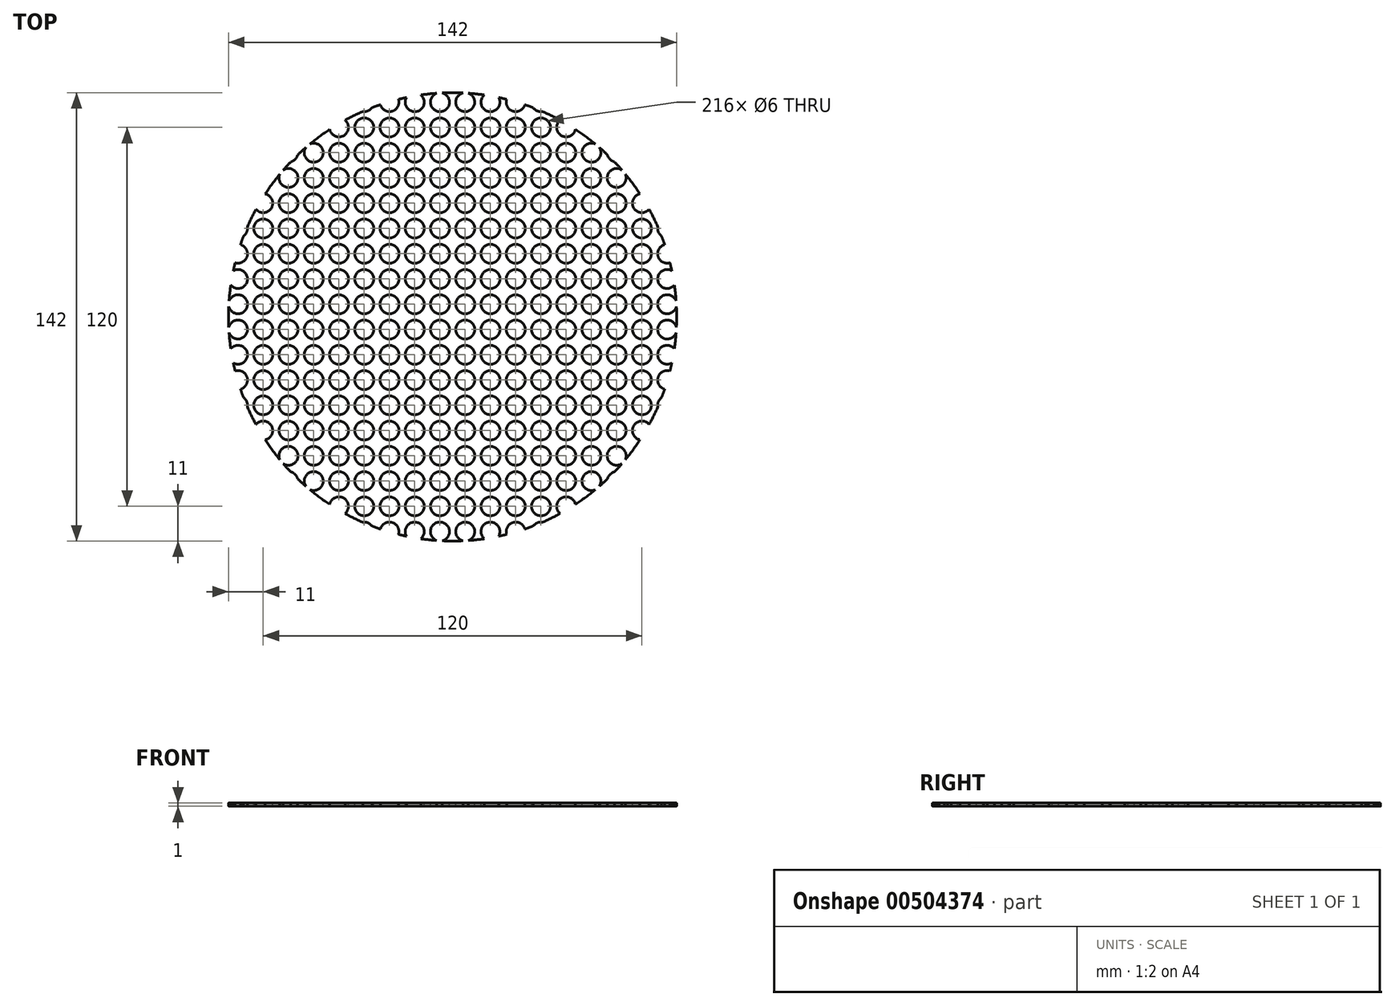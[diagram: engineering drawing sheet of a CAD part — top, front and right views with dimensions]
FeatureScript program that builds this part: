
annotation { "Feature Type Name" : "Feature", "Feature Type Description" : "" }
export const myFeature = defineFeature(function(context is Context, id is Id, definition is map)
    precondition{}
    {
        {
            var Q0;
            Q0=qCreatedBy(makeId("Top.planeOp"),FACE);
            var sketch = newSketch(context, id + "F0", { "sketchPlane" : qUnion([Q0])});
            skCircle(sketch, "E0.0", {"center": v(0, 0) * mm, "radius": 71 * mm});
            skSolve(sketch);
        }
        {
            var Q0;
            Q0 = qSketchRegion(id + "F0", true);
            extrude(context, id + "F1", {"entities" : qUnion([Q0]), "oppositeDirection" : true, "depth" : 1 * mm, "offsetDistance" : 25 * mm});
        }
        {
            var Q0;
            Q0=qCreatedBy(makeId("Top.planeOp"),FACE);
            var sketch = newSketch(context, id + "F2", { "sketchPlane" : qUnion([Q0])});
            skCircle(sketch, "E1", {"center": v(0, 0) * mm, "radius": 71 * mm, "construction": true});
            skLineSegment(sketch, "E2", {"start": v(-4, 70.89) * mm, "end": v(-4, -70.89) * mm, "construction": true});
            skLineSegment(sketch, "E3", {"start": v(-12, 69.98) * mm, "end": v(-12, -69.98) * mm, "construction": true});
            skLineSegment(sketch, "E4", {"start": v(-20, 68.12) * mm, "end": v(-20, -68.12) * mm, "construction": true});
            skLineSegment(sketch, "E5", {"start": v(-28, 65.25) * mm, "end": v(-28, -65.25) * mm, "construction": true});
            skLineSegment(sketch, "E6.MirrorCS", {"start": v(-36, 68.12) * mm, "end": v(-36, -68.12) * mm, "construction": true});
            skLineSegment(sketch, "E7.MirrorCS", {"start": v(-44, 69.98) * mm, "end": v(-44, -69.98) * mm, "construction": true});
            skLineSegment(sketch, "E8.MirrorCS", {"start": v(-52, 70.89) * mm, "end": v(-52, -70.89) * mm, "construction": true});
            skLineSegment(sketch, "E9.MirrorCS", {"start": v(-60, 69.98) * mm, "end": v(-60, -69.98) * mm, "construction": true});
            skLineSegment(sketch, "E10.MirrorCS", {"start": v(-68, 68.12) * mm, "end": v(-68, -68.12) * mm, "construction": true});
            skLineSegment(sketch, "E11.MirrorCS", {"start": v(4, 70.89) * mm, "end": v(4, -70.89) * mm, "construction": true});
            skLineSegment(sketch, "E12.MirrorCS", {"start": v(12, 69.98) * mm, "end": v(12, -69.98) * mm, "construction": true});
            skLineSegment(sketch, "E13.MirrorCS", {"start": v(20, 68.12) * mm, "end": v(20, -68.12) * mm, "construction": true});
            skLineSegment(sketch, "E14.MirrorCS", {"start": v(28, 65.25) * mm, "end": v(28, -65.25) * mm, "construction": true});
            skLineSegment(sketch, "E15.MirrorCS", {"start": v(36, 68.12) * mm, "end": v(36, -68.12) * mm, "construction": true});
            skLineSegment(sketch, "E16.MirrorCS", {"start": v(44, 69.98) * mm, "end": v(44, -69.98) * mm, "construction": true});
            skLineSegment(sketch, "E17.MirrorCS", {"start": v(52, 70.89) * mm, "end": v(52, -70.89) * mm, "construction": true});
            skLineSegment(sketch, "E18.MirrorCS", {"start": v(60, 69.98) * mm, "end": v(60, -69.98) * mm, "construction": true});
            skLineSegment(sketch, "E19.MirrorCS", {"start": v(68, 68.12) * mm, "end": v(68, -68.12) * mm, "construction": true});
            skLineSegment(sketch, "E20", {"start": v(-70.89, 4) * mm, "end": v(70.89, 4) * mm, "construction": true});
            skLineSegment(sketch, "E21", {"start": v(-69.98, 12) * mm, "end": v(69.98, 12) * mm, "construction": true});
            skLineSegment(sketch, "E22", {"start": v(-68.12, 20) * mm, "end": v(68.12, 20) * mm});
            skLineSegment(sketch, "E23.MirrorCS", {"start": v(-69.98, 28) * mm, "end": v(69.98, 28) * mm, "construction": true});
            skLineSegment(sketch, "E24.MirrorCS", {"start": v(-70.89, 36) * mm, "end": v(70.89, 36) * mm, "construction": true});
            skLineSegment(sketch, "E25.MirrorCS", {"start": v(-69.98, 44) * mm, "end": v(69.98, 44) * mm, "construction": true});
            skLineSegment(sketch, "E26.MirrorCS", {"start": v(-68.12, 52) * mm, "end": v(68.12, 52) * mm, "construction": true});
            skLineSegment(sketch, "E27.MirrorCS", {"start": v(-69.98, 60) * mm, "end": v(69.98, 60) * mm, "construction": true});
            skLineSegment(sketch, "E28.MirrorCS", {"start": v(-70.89, 68) * mm, "end": v(70.89, 68) * mm, "construction": true});
            skLineSegment(sketch, "E29.MirrorCS", {"start": v(-69.98, -12) * mm, "end": v(69.98, -12) * mm, "construction": true});
            skLineSegment(sketch, "E30.MirrorCS", {"start": v(-68.12, -20) * mm, "end": v(68.12, -20) * mm, "construction": true});
            skLineSegment(sketch, "E31.MirrorCS", {"start": v(-69.98, -28) * mm, "end": v(69.98, -28) * mm, "construction": true});
            skLineSegment(sketch, "E32.MirrorCS", {"start": v(-70.89, -36) * mm, "end": v(70.89, -36) * mm, "construction": true});
            skLineSegment(sketch, "E33.MirrorCS", {"start": v(-69.98, -44) * mm, "end": v(69.98, -44) * mm, "construction": true});
            skLineSegment(sketch, "E34.MirrorCS", {"start": v(-68.12, -52) * mm, "end": v(68.12, -52) * mm, "construction": true});
            skLineSegment(sketch, "E35.MirrorCS", {"start": v(-69.98, -60) * mm, "end": v(69.98, -60) * mm, "construction": true});
            skLineSegment(sketch, "E36.MirrorCS", {"start": v(-70.89, -68) * mm, "end": v(70.89, -68) * mm, "construction": true});
            skLineSegment(sketch, "E37.MirrorCS", {"start": v(-70.89, -4) * mm, "end": v(70.89, -4) * mm, "construction": true});
            skCircle(sketch, "E38", {"center": v(-12, 4) * mm, "radius": 3 * mm});
            skCircle(sketch, "E39.MirrorC", {"center": v(-28, 4) * mm, "radius": 3 * mm});
            skCircle(sketch, "E40", {"center": v(-20, 4) * mm, "radius": 3 * mm});
            skCircle(sketch, "E41.MirrorC", {"center": v(-36, 4) * mm, "radius": 3 * mm});
            skCircle(sketch, "E42.MirrorC", {"center": v(-44, 4) * mm, "radius": 3 * mm});
            skCircle(sketch, "E43.MirrorC", {"center": v(-52, 4) * mm, "radius": 3 * mm});
            skCircle(sketch, "E44.MirrorC", {"center": v(-60, 4) * mm, "radius": 3 * mm});
            skCircle(sketch, "E45.MirrorC", {"center": v(-68, 4) * mm, "radius": 3 * mm});
            skCircle(sketch, "E46.MirrorC", {"center": v(-4, 4) * mm, "radius": 3 * mm});
            skCircle(sketch, "E47.MirrorC", {"center": v(-4, -4) * mm, "radius": 3 * mm});
            skCircle(sketch, "E48.MirrorC", {"center": v(-12, -4) * mm, "radius": 3 * mm});
            skCircle(sketch, "E49.MirrorC", {"center": v(-20, -4) * mm, "radius": 3 * mm});
            skCircle(sketch, "E50.MirrorC", {"center": v(-28, -4) * mm, "radius": 3 * mm});
            skCircle(sketch, "E51.MirrorC", {"center": v(-36, -4) * mm, "radius": 3 * mm});
            skCircle(sketch, "E52.MirrorC", {"center": v(-44, -4) * mm, "radius": 3 * mm});
            skCircle(sketch, "E53.MirrorC", {"center": v(-52, -4) * mm, "radius": 3 * mm});
            skCircle(sketch, "E54.MirrorC", {"center": v(-60, -4) * mm, "radius": 3 * mm});
            skCircle(sketch, "E55.MirrorC", {"center": v(-68, -4) * mm, "radius": 3 * mm});
            skCircle(sketch, "E56.MirrorC", {"center": v(-4, 20) * mm, "radius": 3 * mm});
            skCircle(sketch, "E57.MirrorC", {"center": v(-4, 28) * mm, "radius": 3 * mm});
            skCircle(sketch, "E58.MirrorC", {"center": v(-12, 28) * mm, "radius": 3 * mm});
            skCircle(sketch, "E59.MirrorC", {"center": v(-12, 20) * mm, "radius": 3 * mm});
            skCircle(sketch, "E60.MirrorC", {"center": v(-20, 20) * mm, "radius": 3 * mm});
            skCircle(sketch, "E61.MirrorC", {"center": v(-20, 28) * mm, "radius": 3 * mm});
            skCircle(sketch, "E62.MirrorC", {"center": v(-28, 20) * mm, "radius": 3 * mm});
            skCircle(sketch, "E63.MirrorC", {"center": v(-28, 28) * mm, "radius": 3 * mm});
            skCircle(sketch, "E64.MirrorC", {"center": v(-36, 20) * mm, "radius": 3 * mm});
            skCircle(sketch, "E65.MirrorC", {"center": v(-36, 28) * mm, "radius": 3 * mm});
            skCircle(sketch, "E66.MirrorC", {"center": v(-44, 20) * mm, "radius": 3 * mm});
            skCircle(sketch, "E67.MirrorC", {"center": v(-44, 28) * mm, "radius": 3 * mm});
            skCircle(sketch, "E68.MirrorC", {"center": v(-52, 28) * mm, "radius": 3 * mm});
            skCircle(sketch, "E69.MirrorC", {"center": v(-52, 20) * mm, "radius": 3 * mm});
            skCircle(sketch, "E70.MirrorC", {"center": v(-60, 20) * mm, "radius": 3 * mm});
            skCircle(sketch, "E71.MirrorC", {"center": v(-68, 20) * mm, "radius": 3 * mm});
            skCircle(sketch, "E72.MirrorC", {"center": v(-4, 12) * mm, "radius": 3 * mm});
            skCircle(sketch, "E73.MirrorC", {"center": v(-12, 12) * mm, "radius": 3 * mm});
            skCircle(sketch, "E74.MirrorC", {"center": v(-20, 12) * mm, "radius": 3 * mm});
            skCircle(sketch, "E75.MirrorC", {"center": v(-28, 12) * mm, "radius": 3 * mm});
            skCircle(sketch, "E76.MirrorC", {"center": v(-36, 12) * mm, "radius": 3 * mm});
            skCircle(sketch, "E77.MirrorC", {"center": v(-44, 12) * mm, "radius": 3 * mm});
            skCircle(sketch, "E78.MirrorC", {"center": v(-52, 12) * mm, "radius": 3 * mm});
            skCircle(sketch, "E79.MirrorC", {"center": v(-60, 12) * mm, "radius": 3 * mm});
            skLineSegment(sketch, "E80.MirrorCS", {"start": v(-60, -61.98) * mm, "end": v(-60, 77.98) * mm, "construction": true});
            skCircle(sketch, "E81.MirrorC", {"center": v(-68, 12) * mm, "radius": 3 * mm});
            skCircle(sketch, "E82.MirrorC", {"center": v(-68, 28) * mm, "radius": 3 * mm});
            skCircle(sketch, "E83.MirrorC", {"center": v(-60, 28) * mm, "radius": 3 * mm});
            skCircle(sketch, "E84.MirrorC", {"center": v(-52, 44) * mm, "radius": 3 * mm});
            skCircle(sketch, "E85.MirrorC", {"center": v(-36, 44) * mm, "radius": 3 * mm});
            skCircle(sketch, "E86.MirrorC", {"center": v(-52, 36) * mm, "radius": 3 * mm});
            skCircle(sketch, "E87.MirrorC", {"center": v(-44, 36) * mm, "radius": 3 * mm});
            skCircle(sketch, "E88.MirrorC", {"center": v(-44, 44) * mm, "radius": 3 * mm});
            skCircle(sketch, "E89.MirrorC", {"center": v(-28, 44) * mm, "radius": 3 * mm});
            skCircle(sketch, "E90.MirrorC", {"center": v(-60, 36) * mm, "radius": 3 * mm});
            skCircle(sketch, "E91.MirrorC", {"center": v(-36, 36) * mm, "radius": 3 * mm});
            skCircle(sketch, "E92.MirrorC", {"center": v(-28, 36) * mm, "radius": 3 * mm});
            skCircle(sketch, "E93.MirrorC", {"center": v(-20, 36) * mm, "radius": 3 * mm});
            skCircle(sketch, "E94.MirrorC", {"center": v(-68, 44) * mm, "radius": 3 * mm});
            skCircle(sketch, "E95.MirrorC", {"center": v(-4, 36) * mm, "radius": 3 * mm});
            skCircle(sketch, "E96.MirrorC", {"center": v(-60, 44) * mm, "radius": 3 * mm});
            skCircle(sketch, "E97.MirrorC", {"center": v(-12, 36) * mm, "radius": 3 * mm});
            skCircle(sketch, "E98.MirrorC", {"center": v(-4, 44) * mm, "radius": 3 * mm});
            skCircle(sketch, "E99.MirrorC", {"center": v(-12, 44) * mm, "radius": 3 * mm});
            skCircle(sketch, "E100.MirrorC", {"center": v(-20, 44) * mm, "radius": 3 * mm});
            skCircle(sketch, "E101.MirrorC", {"center": v(-68, 36) * mm, "radius": 3 * mm});
            skCircle(sketch, "E102.MirrorC", {"center": v(-4, 60) * mm, "radius": 3 * mm});
            skCircle(sketch, "E103.MirrorC", {"center": v(-68, 60) * mm, "radius": 3 * mm});
            skCircle(sketch, "E104.MirrorC", {"center": v(-52, 60) * mm, "radius": 3 * mm});
            skCircle(sketch, "E105.MirrorC", {"center": v(-44, 60) * mm, "radius": 3 * mm});
            skCircle(sketch, "E106.MirrorC", {"center": v(-36, 60) * mm, "radius": 3 * mm});
            skCircle(sketch, "E107.MirrorC", {"center": v(-20, 60) * mm, "radius": 3 * mm});
            skCircle(sketch, "E108.MirrorC", {"center": v(-60, 60) * mm, "radius": 3 * mm});
            skCircle(sketch, "E109.MirrorC", {"center": v(-28, 60) * mm, "radius": 3 * mm});
            skCircle(sketch, "E110.MirrorC", {"center": v(-12, 60) * mm, "radius": 3 * mm});
            skCircle(sketch, "E111.MirrorC", {"center": v(-36, 52) * mm, "radius": 3 * mm});
            skCircle(sketch, "E112.MirrorC", {"center": v(-68, 52) * mm, "radius": 3 * mm});
            skCircle(sketch, "E113.MirrorC", {"center": v(-44, 68) * mm, "radius": 3 * mm});
            skCircle(sketch, "E114.MirrorC", {"center": v(-52, 52) * mm, "radius": 3 * mm});
            skCircle(sketch, "E115.MirrorC", {"center": v(-4, 52) * mm, "radius": 3 * mm});
            skCircle(sketch, "E116.MirrorC", {"center": v(-12, 68) * mm, "radius": 3 * mm});
            skCircle(sketch, "E117.MirrorC", {"center": v(-12, 52) * mm, "radius": 3 * mm});
            skCircle(sketch, "E118.MirrorC", {"center": v(-4, 68) * mm, "radius": 3 * mm});
            skCircle(sketch, "E119.MirrorC", {"center": v(-60, 52) * mm, "radius": 3 * mm});
            skCircle(sketch, "E120.MirrorC", {"center": v(-60, 68) * mm, "radius": 3 * mm});
            skCircle(sketch, "E121.MirrorC", {"center": v(-52, 68) * mm, "radius": 3 * mm});
            skCircle(sketch, "E122.MirrorC", {"center": v(-28, 52) * mm, "radius": 3 * mm});
            skCircle(sketch, "E123.MirrorC", {"center": v(-28, 68) * mm, "radius": 3 * mm});
            skCircle(sketch, "E124.MirrorC", {"center": v(-68, 68) * mm, "radius": 3 * mm});
            skCircle(sketch, "E125.MirrorC", {"center": v(-36, 68) * mm, "radius": 3 * mm});
            skCircle(sketch, "E126.MirrorC", {"center": v(-44, 52) * mm, "radius": 3 * mm});
            skCircle(sketch, "E127.MirrorC", {"center": v(-20, 68) * mm, "radius": 3 * mm});
            skCircle(sketch, "E128.MirrorC", {"center": v(-20, 52) * mm, "radius": 3 * mm});
            skCircle(sketch, "E129.MirrorC", {"center": v(52, -4) * mm, "radius": 3 * mm});
            skCircle(sketch, "E130.MirrorC", {"center": v(52, 44) * mm, "radius": 3 * mm});
            skCircle(sketch, "E131.MirrorC", {"center": v(44, 28) * mm, "radius": 3 * mm});
            skCircle(sketch, "E132.MirrorC", {"center": v(68, 28) * mm, "radius": 3 * mm});
            skCircle(sketch, "E133.MirrorC", {"center": v(52, 28) * mm, "radius": 3 * mm});
            skCircle(sketch, "E134.MirrorC", {"center": v(68, 60) * mm, "radius": 3 * mm});
            skCircle(sketch, "E135.MirrorC", {"center": v(36, 28) * mm, "radius": 3 * mm});
            skCircle(sketch, "E136.MirrorC", {"center": v(4, 60) * mm, "radius": 3 * mm});
            skCircle(sketch, "E137.MirrorC", {"center": v(60, 28) * mm, "radius": 3 * mm});
            skCircle(sketch, "E138.MirrorC", {"center": v(36, 60) * mm, "radius": 3 * mm});
            skCircle(sketch, "E139.MirrorC", {"center": v(28, 28) * mm, "radius": 3 * mm});
            skCircle(sketch, "E140.MirrorC", {"center": v(52, 60) * mm, "radius": 3 * mm});
            skCircle(sketch, "E141.MirrorC", {"center": v(12, 60) * mm, "radius": 3 * mm});
            skCircle(sketch, "E142.MirrorC", {"center": v(4, 28) * mm, "radius": 3 * mm});
            skCircle(sketch, "E143.MirrorC", {"center": v(60, 60) * mm, "radius": 3 * mm});
            skCircle(sketch, "E144.MirrorC", {"center": v(44, 60) * mm, "radius": 3 * mm});
            skCircle(sketch, "E145.MirrorC", {"center": v(12, 28) * mm, "radius": 3 * mm});
            skCircle(sketch, "E146.MirrorC", {"center": v(28, 60) * mm, "radius": 3 * mm});
            skCircle(sketch, "E147.MirrorC", {"center": v(20, 28) * mm, "radius": 3 * mm});
            skCircle(sketch, "E148.MirrorC", {"center": v(20, 60) * mm, "radius": 3 * mm});
            skCircle(sketch, "E149.MirrorC", {"center": v(52, 52) * mm, "radius": 3 * mm});
            skCircle(sketch, "E150.MirrorC", {"center": v(36, 68) * mm, "radius": 3 * mm});
            skCircle(sketch, "E151.MirrorC", {"center": v(36, -4) * mm, "radius": 3 * mm});
            skCircle(sketch, "E152.MirrorC", {"center": v(68, 12) * mm, "radius": 3 * mm});
            skCircle(sketch, "E153.MirrorC", {"center": v(36, 36) * mm, "radius": 3 * mm});
            skCircle(sketch, "E154.MirrorC", {"center": v(68, 36) * mm, "radius": 3 * mm});
            skCircle(sketch, "E155.MirrorC", {"center": v(44, 68) * mm, "radius": 3 * mm});
            skCircle(sketch, "E156.MirrorC", {"center": v(68, 68) * mm, "radius": 3 * mm});
            skCircle(sketch, "E157.MirrorC", {"center": v(28, -4) * mm, "radius": 3 * mm});
            skCircle(sketch, "E158.MirrorC", {"center": v(44, 20) * mm, "radius": 3 * mm});
            skCircle(sketch, "E159.MirrorC", {"center": v(20, -4) * mm, "radius": 3 * mm});
            skCircle(sketch, "E160.MirrorC", {"center": v(60, 36) * mm, "radius": 3 * mm});
            skCircle(sketch, "E161.MirrorC", {"center": v(68, 52) * mm, "radius": 3 * mm});
            skCircle(sketch, "E162.MirrorC", {"center": v(44, -4) * mm, "radius": 3 * mm});
            skCircle(sketch, "E163.MirrorC", {"center": v(44, 52) * mm, "radius": 3 * mm});
            skCircle(sketch, "E164.MirrorC", {"center": v(4, 52) * mm, "radius": 3 * mm});
            skCircle(sketch, "E165.MirrorC", {"center": v(20, 20) * mm, "radius": 3 * mm});
            skCircle(sketch, "E166.MirrorC", {"center": v(60, 4) * mm, "radius": 3 * mm});
            skCircle(sketch, "E167.MirrorC", {"center": v(4, 44) * mm, "radius": 3 * mm});
            skCircle(sketch, "E168.MirrorC", {"center": v(44, 36) * mm, "radius": 3 * mm});
            skCircle(sketch, "E169.MirrorC", {"center": v(36, 12) * mm, "radius": 3 * mm});
            skCircle(sketch, "E170.MirrorC", {"center": v(60, 68) * mm, "radius": 3 * mm});
            skCircle(sketch, "E171.MirrorC", {"center": v(52, 12) * mm, "radius": 3 * mm});
            skCircle(sketch, "E172.MirrorC", {"center": v(28, 20) * mm, "radius": 3 * mm});
            skCircle(sketch, "E173.MirrorC", {"center": v(4, 4) * mm, "radius": 3 * mm});
            skCircle(sketch, "E174.MirrorC", {"center": v(28, 52) * mm, "radius": 3 * mm});
            skCircle(sketch, "E175.MirrorC", {"center": v(52, 20) * mm, "radius": 3 * mm});
            skCircle(sketch, "E176.MirrorC", {"center": v(12, 44) * mm, "radius": 3 * mm});
            skCircle(sketch, "E177.MirrorC", {"center": v(20, 68) * mm, "radius": 3 * mm});
            skCircle(sketch, "E178.MirrorC", {"center": v(28, 44) * mm, "radius": 3 * mm});
            skCircle(sketch, "E179.MirrorC", {"center": v(12, 36) * mm, "radius": 3 * mm});
            skCircle(sketch, "E180.MirrorC", {"center": v(52, 4) * mm, "radius": 3 * mm});
            skCircle(sketch, "E181.MirrorC", {"center": v(12, 20) * mm, "radius": 3 * mm});
            skCircle(sketch, "E182.MirrorC", {"center": v(28, 68) * mm, "radius": 3 * mm});
            skCircle(sketch, "E183.MirrorC", {"center": v(4, 68) * mm, "radius": 3 * mm});
            skCircle(sketch, "E184.MirrorC", {"center": v(36, 4) * mm, "radius": 3 * mm});
            skCircle(sketch, "E185.MirrorC", {"center": v(4, -4) * mm, "radius": 3 * mm});
            skCircle(sketch, "E186.MirrorC", {"center": v(12, 12) * mm, "radius": 3 * mm});
            skCircle(sketch, "E187.MirrorC", {"center": v(52, 36) * mm, "radius": 3 * mm});
            skCircle(sketch, "E188.MirrorC", {"center": v(60, 52) * mm, "radius": 3 * mm});
            skCircle(sketch, "E189.MirrorC", {"center": v(4, 36) * mm, "radius": 3 * mm});
            skCircle(sketch, "E190.MirrorC", {"center": v(60, 20) * mm, "radius": 3 * mm});
            skCircle(sketch, "E191.MirrorC", {"center": v(60, -4) * mm, "radius": 3 * mm});
            skCircle(sketch, "E192.MirrorC", {"center": v(36, 20) * mm, "radius": 3 * mm});
            skCircle(sketch, "E193.MirrorC", {"center": v(28, 12) * mm, "radius": 3 * mm});
            skCircle(sketch, "E194.MirrorC", {"center": v(28, 36) * mm, "radius": 3 * mm});
            skCircle(sketch, "E195.MirrorC", {"center": v(68, 20) * mm, "radius": 3 * mm});
            skCircle(sketch, "E196.MirrorC", {"center": v(12, -4) * mm, "radius": 3 * mm});
            skCircle(sketch, "E197.MirrorC", {"center": v(44, 12) * mm, "radius": 3 * mm});
            skCircle(sketch, "E198.MirrorC", {"center": v(20, 52) * mm, "radius": 3 * mm});
            skCircle(sketch, "E199.MirrorC", {"center": v(60, 44) * mm, "radius": 3 * mm});
            skCircle(sketch, "E200.MirrorC", {"center": v(4, 20) * mm, "radius": 3 * mm});
            skCircle(sketch, "E201.MirrorC", {"center": v(20, 4) * mm, "radius": 3 * mm});
            skCircle(sketch, "E202.MirrorC", {"center": v(36, 44) * mm, "radius": 3 * mm});
            skCircle(sketch, "E203.MirrorC", {"center": v(44, 44) * mm, "radius": 3 * mm});
            skCircle(sketch, "E204.MirrorC", {"center": v(68, 4) * mm, "radius": 3 * mm});
            skCircle(sketch, "E205.MirrorC", {"center": v(20, 44) * mm, "radius": 3 * mm});
            skCircle(sketch, "E206.MirrorC", {"center": v(4, 12) * mm, "radius": 3 * mm});
            skCircle(sketch, "E207.MirrorC", {"center": v(68, 44) * mm, "radius": 3 * mm});
            skCircle(sketch, "E208.MirrorC", {"center": v(12, 4) * mm, "radius": 3 * mm});
            skCircle(sketch, "E209.MirrorC", {"center": v(28, 4) * mm, "radius": 3 * mm});
            skCircle(sketch, "E210.MirrorC", {"center": v(60, 12) * mm, "radius": 3 * mm});
            skCircle(sketch, "E211.MirrorC", {"center": v(36, 52) * mm, "radius": 3 * mm});
            skCircle(sketch, "E212.MirrorC", {"center": v(52, 68) * mm, "radius": 3 * mm});
            skCircle(sketch, "E213.MirrorC", {"center": v(20, 12) * mm, "radius": 3 * mm});
            skCircle(sketch, "E214.MirrorC", {"center": v(68, -4) * mm, "radius": 3 * mm});
            skCircle(sketch, "E215.MirrorC", {"center": v(20, 36) * mm, "radius": 3 * mm});
            skCircle(sketch, "E216.MirrorC", {"center": v(44, 4) * mm, "radius": 3 * mm});
            skCircle(sketch, "E217.MirrorC", {"center": v(12, 52) * mm, "radius": 3 * mm});
            skCircle(sketch, "E218.MirrorC", {"center": v(12, 68) * mm, "radius": 3 * mm});
            skLineSegment(sketch, "E219.MirrorCS", {"start": v(70.89, -4) * mm, "end": v(-70.89, -4) * mm});
            skCircle(sketch, "E220.MirrorC", {"center": v(-52, -52) * mm, "radius": 3 * mm});
            skCircle(sketch, "E221.MirrorC", {"center": v(52, -52) * mm, "radius": 3 * mm});
            skCircle(sketch, "E222.MirrorC", {"center": v(-68, -68) * mm, "radius": 3 * mm});
            skCircle(sketch, "E223.MirrorC", {"center": v(4, -68) * mm, "radius": 3 * mm});
            skCircle(sketch, "E224.MirrorC", {"center": v(36, -36) * mm, "radius": 3 * mm});
            skCircle(sketch, "E225.MirrorC", {"center": v(20, -36) * mm, "radius": 3 * mm});
            skCircle(sketch, "E226.MirrorC", {"center": v(-28, -36) * mm, "radius": 3 * mm});
            skCircle(sketch, "E227.MirrorC", {"center": v(-12, -68) * mm, "radius": 3 * mm});
            skCircle(sketch, "E228.MirrorC", {"center": v(-20, -36) * mm, "radius": 3 * mm});
            skCircle(sketch, "E229.MirrorC", {"center": v(52, -68) * mm, "radius": 3 * mm});
            skCircle(sketch, "E230.MirrorC", {"center": v(-20, -68) * mm, "radius": 3 * mm});
            skCircle(sketch, "E231.MirrorC", {"center": v(-12, -36) * mm, "radius": 3 * mm});
            skCircle(sketch, "E232.MirrorC", {"center": v(60, -36) * mm, "radius": 3 * mm});
            skCircle(sketch, "E233.MirrorC", {"center": v(28, -68) * mm, "radius": 3 * mm});
            skCircle(sketch, "E234.MirrorC", {"center": v(-52, -68) * mm, "radius": 3 * mm});
            skCircle(sketch, "E235.MirrorC", {"center": v(-44, -36) * mm, "radius": 3 * mm});
            skCircle(sketch, "E236.MirrorC", {"center": v(36, -68) * mm, "radius": 3 * mm});
            skCircle(sketch, "E237.MirrorC", {"center": v(-36, -36) * mm, "radius": 3 * mm});
            skCircle(sketch, "E238.MirrorC", {"center": v(52, -36) * mm, "radius": 3 * mm});
            skCircle(sketch, "E239.MirrorC", {"center": v(44, -36) * mm, "radius": 3 * mm});
            skCircle(sketch, "E240.MirrorC", {"center": v(28, -36) * mm, "radius": 3 * mm});
            skCircle(sketch, "E241.MirrorC", {"center": v(44, -68) * mm, "radius": 3 * mm});
            skCircle(sketch, "E242.MirrorC", {"center": v(-4, -68) * mm, "radius": 3 * mm});
            skCircle(sketch, "E243.MirrorC", {"center": v(-4, -36) * mm, "radius": 3 * mm});
            skCircle(sketch, "E244.MirrorC", {"center": v(-68, -36) * mm, "radius": 3 * mm});
            skCircle(sketch, "E245.MirrorC", {"center": v(-52, -36) * mm, "radius": 3 * mm});
            skCircle(sketch, "E246.MirrorC", {"center": v(12, -68) * mm, "radius": 3 * mm});
            skCircle(sketch, "E247.MirrorC", {"center": v(-60, -36) * mm, "radius": 3 * mm});
            skCircle(sketch, "E248.MirrorC", {"center": v(-36, -68) * mm, "radius": 3 * mm});
            skCircle(sketch, "E249.MirrorC", {"center": v(4, -36) * mm, "radius": 3 * mm});
            skCircle(sketch, "E250.MirrorC", {"center": v(12, -36) * mm, "radius": 3 * mm});
            skCircle(sketch, "E251.MirrorC", {"center": v(-60, -68) * mm, "radius": 3 * mm});
            skCircle(sketch, "E252.MirrorC", {"center": v(68, -68) * mm, "radius": 3 * mm});
            skCircle(sketch, "E253.MirrorC", {"center": v(68, -36) * mm, "radius": 3 * mm});
            skCircle(sketch, "E254.MirrorC", {"center": v(-44, -68) * mm, "radius": 3 * mm});
            skCircle(sketch, "E255.MirrorC", {"center": v(-28, -68) * mm, "radius": 3 * mm});
            skCircle(sketch, "E256.MirrorC", {"center": v(20, -68) * mm, "radius": 3 * mm});
            skCircle(sketch, "E257.MirrorC", {"center": v(60, -68) * mm, "radius": 3 * mm});
            skCircle(sketch, "E258.MirrorC", {"center": v(-52, -20) * mm, "radius": 3 * mm});
            skCircle(sketch, "E259.MirrorC", {"center": v(-28, -28) * mm, "radius": 3 * mm});
            skCircle(sketch, "E260.MirrorC", {"center": v(-28, -60) * mm, "radius": 3 * mm});
            skCircle(sketch, "E261.MirrorC", {"center": v(-12, -52) * mm, "radius": 3 * mm});
            skCircle(sketch, "E262.MirrorC", {"center": v(-28, -52) * mm, "radius": 3 * mm});
            skCircle(sketch, "E263.MirrorC", {"center": v(52, -28) * mm, "radius": 3 * mm});
            skCircle(sketch, "E264.MirrorC", {"center": v(68, -60) * mm, "radius": 3 * mm});
            skCircle(sketch, "E265.MirrorC", {"center": v(52, -76) * mm, "radius": 3 * mm});
            skCircle(sketch, "E266.MirrorC", {"center": v(4, -28) * mm, "radius": 3 * mm});
            skCircle(sketch, "E267.MirrorC", {"center": v(-60, -20) * mm, "radius": 3 * mm});
            skCircle(sketch, "E268.MirrorC", {"center": v(-28, -76) * mm, "radius": 3 * mm});
            skCircle(sketch, "E269.MirrorC", {"center": v(12, -52) * mm, "radius": 3 * mm});
            skCircle(sketch, "E270.MirrorC", {"center": v(52, -60) * mm, "radius": 3 * mm});
            skCircle(sketch, "E271.MirrorC", {"center": v(20, -20) * mm, "radius": 3 * mm});
            skCircle(sketch, "E272.MirrorC", {"center": v(60, -60) * mm, "radius": 3 * mm});
            skCircle(sketch, "E273.MirrorC", {"center": v(-36, -28) * mm, "radius": 3 * mm});
            skCircle(sketch, "E274.MirrorC", {"center": v(-36, -60) * mm, "radius": 3 * mm});
            skCircle(sketch, "E275.MirrorC", {"center": v(-20, -52) * mm, "radius": 3 * mm});
            skCircle(sketch, "E276.MirrorC", {"center": v(20, -76) * mm, "radius": 3 * mm});
            skCircle(sketch, "E277.MirrorC", {"center": v(36, -76) * mm, "radius": 3 * mm});
            skCircle(sketch, "E278.MirrorC", {"center": v(36, -52) * mm, "radius": 3 * mm});
            skCircle(sketch, "E279.MirrorC", {"center": v(4, -44) * mm, "radius": 3 * mm});
            skCircle(sketch, "E280.MirrorC", {"center": v(-68, -60) * mm, "radius": 3 * mm});
            skCircle(sketch, "E281.MirrorC", {"center": v(-60, -44) * mm, "radius": 3 * mm});
            skCircle(sketch, "E282.MirrorC", {"center": v(28, -52) * mm, "radius": 3 * mm});
            skCircle(sketch, "E283.MirrorC", {"center": v(44, -60) * mm, "radius": 3 * mm});
            skCircle(sketch, "E284.MirrorC", {"center": v(44, -52) * mm, "radius": 3 * mm});
            skCircle(sketch, "E285.MirrorC", {"center": v(60, -28) * mm, "radius": 3 * mm});
            skCircle(sketch, "E286.MirrorC", {"center": v(4, -60) * mm, "radius": 3 * mm});
            skCircle(sketch, "E287.MirrorC", {"center": v(20, -44) * mm, "radius": 3 * mm});
            skCircle(sketch, "E288.MirrorC", {"center": v(-44, -28) * mm, "radius": 3 * mm});
            skCircle(sketch, "E289.MirrorC", {"center": v(-68, -76) * mm, "radius": 3 * mm});
            skCircle(sketch, "E290.MirrorC", {"center": v(-44, -76) * mm, "radius": 3 * mm});
            skCircle(sketch, "E291.MirrorC", {"center": v(-68, -44) * mm, "radius": 3 * mm});
            skCircle(sketch, "E292.MirrorC", {"center": v(-36, -44) * mm, "radius": 3 * mm});
            skCircle(sketch, "E293.MirrorC", {"center": v(36, -28) * mm, "radius": 3 * mm});
            skCircle(sketch, "E294.MirrorC", {"center": v(-68, -20) * mm, "radius": 3 * mm});
            skCircle(sketch, "E295.MirrorC", {"center": v(-36, -76) * mm, "radius": 3 * mm});
            skCircle(sketch, "E296.MirrorC", {"center": v(-52, -60) * mm, "radius": 3 * mm});
            skCircle(sketch, "E297.MirrorC", {"center": v(12, -44) * mm, "radius": 3 * mm});
            skCircle(sketch, "E298.MirrorC", {"center": v(20, -28) * mm, "radius": 3 * mm});
            skCircle(sketch, "E299.MirrorC", {"center": v(68, -20) * mm, "radius": 3 * mm});
            skLineSegment(sketch, "E300.MirrorCS", {"start": v(-70.89, -12) * mm, "end": v(70.89, -12) * mm, "construction": true});
            skCircle(sketch, "E301.MirrorC", {"center": v(-44, -60) * mm, "radius": 3 * mm});
            skCircle(sketch, "E302.MirrorC", {"center": v(-4, -60) * mm, "radius": 3 * mm});
            skCircle(sketch, "E303.MirrorC", {"center": v(36, -44) * mm, "radius": 3 * mm});
            skCircle(sketch, "E304.MirrorC", {"center": v(12, -60) * mm, "radius": 3 * mm});
            skCircle(sketch, "E305.MirrorC", {"center": v(20, -52) * mm, "radius": 3 * mm});
            skCircle(sketch, "E306.MirrorC", {"center": v(28, -20) * mm, "radius": 3 * mm});
            skLineSegment(sketch, "E307.MirrorCS", {"start": v(-69.98, -20) * mm, "end": v(69.98, -20) * mm});
            skCircle(sketch, "E308.MirrorC", {"center": v(-52, -28) * mm, "radius": 3 * mm});
            skCircle(sketch, "E309.MirrorC", {"center": v(-20, -76) * mm, "radius": 3 * mm});
            skCircle(sketch, "E310.MirrorC", {"center": v(12, -28) * mm, "radius": 3 * mm});
            skCircle(sketch, "E311.MirrorC", {"center": v(4, -52) * mm, "radius": 3 * mm});
            skCircle(sketch, "E312.MirrorC", {"center": v(68, -44) * mm, "radius": 3 * mm});
            skCircle(sketch, "E313.MirrorC", {"center": v(12, -76) * mm, "radius": 3 * mm});
            skCircle(sketch, "E314.MirrorC", {"center": v(4, -20) * mm, "radius": 3 * mm});
            skCircle(sketch, "E315.MirrorC", {"center": v(28, -44) * mm, "radius": 3 * mm});
            skCircle(sketch, "E316.MirrorC", {"center": v(60, -76) * mm, "radius": 3 * mm});
            skCircle(sketch, "E317.MirrorC", {"center": v(44, -20) * mm, "radius": 3 * mm});
            skCircle(sketch, "E318.MirrorC", {"center": v(-4, -76) * mm, "radius": 3 * mm});
            skCircle(sketch, "E319.MirrorC", {"center": v(-4, -20) * mm, "radius": 3 * mm});
            skCircle(sketch, "E320.MirrorC", {"center": v(-36, -52) * mm, "radius": 3 * mm});
            skCircle(sketch, "E321.MirrorC", {"center": v(-68, -52) * mm, "radius": 3 * mm});
            skLineSegment(sketch, "E322.MirrorCS", {"start": v(-70.89, -44) * mm, "end": v(70.89, -44) * mm, "construction": true});
            skCircle(sketch, "E323.MirrorC", {"center": v(-4, -28) * mm, "radius": 3 * mm});
            skLineSegment(sketch, "E324.MirrorCS", {"start": v(-69.98, -52) * mm, "end": v(69.98, -52) * mm, "construction": true});
            skCircle(sketch, "E325.MirrorC", {"center": v(-4, -44) * mm, "radius": 3 * mm});
            skCircle(sketch, "E326.MirrorC", {"center": v(-44, -52) * mm, "radius": 3 * mm});
            skCircle(sketch, "E327.MirrorC", {"center": v(-44, -20) * mm, "radius": 3 * mm});
            skCircle(sketch, "E328.MirrorC", {"center": v(-52, -44) * mm, "radius": 3 * mm});
            skCircle(sketch, "E329.MirrorC", {"center": v(-12, -20) * mm, "radius": 3 * mm});
            skCircle(sketch, "E330.MirrorC", {"center": v(44, -28) * mm, "radius": 3 * mm});
            skCircle(sketch, "E331.MirrorC", {"center": v(60, -44) * mm, "radius": 3 * mm});
            skCircle(sketch, "E332.MirrorC", {"center": v(-60, -60) * mm, "radius": 3 * mm});
            skCircle(sketch, "E333.MirrorC", {"center": v(-52, -76) * mm, "radius": 3 * mm});
            skCircle(sketch, "E334.MirrorC", {"center": v(52, -44) * mm, "radius": 3 * mm});
            skLineSegment(sketch, "E335.MirrorCS", {"start": v(-68.12, -28) * mm, "end": v(68.12, -28) * mm});
            skCircle(sketch, "E336.MirrorC", {"center": v(36, -20) * mm, "radius": 3 * mm});
            skCircle(sketch, "E337.MirrorC", {"center": v(-60, -28) * mm, "radius": 3 * mm});
            skCircle(sketch, "E338.MirrorC", {"center": v(68, -76) * mm, "radius": 3 * mm});
            skCircle(sketch, "E339.MirrorC", {"center": v(4, -76) * mm, "radius": 3 * mm});
            skCircle(sketch, "E340.MirrorC", {"center": v(-20, -44) * mm, "radius": 3 * mm});
            skCircle(sketch, "E341.MirrorC", {"center": v(-20, -60) * mm, "radius": 3 * mm});
            skCircle(sketch, "E342.MirrorC", {"center": v(-12, -76) * mm, "radius": 3 * mm});
            skCircle(sketch, "E343.MirrorC", {"center": v(52, -20) * mm, "radius": 3 * mm});
            skLineSegment(sketch, "E344.MirrorCS", {"start": v(-68.12, -60) * mm, "end": v(68.12, -60) * mm, "construction": true});
            skCircle(sketch, "E345.MirrorC", {"center": v(-60, -52) * mm, "radius": 3 * mm});
            skCircle(sketch, "E346.MirrorC", {"center": v(-20, -20) * mm, "radius": 3 * mm});
            skCircle(sketch, "E347.MirrorC", {"center": v(20, -60) * mm, "radius": 3 * mm});
            skCircle(sketch, "E348.MirrorC", {"center": v(44, -44) * mm, "radius": 3 * mm});
            skCircle(sketch, "E349.MirrorC", {"center": v(-28, -44) * mm, "radius": 3 * mm});
            skCircle(sketch, "E350.MirrorC", {"center": v(28, -76) * mm, "radius": 3 * mm});
            skCircle(sketch, "E351.MirrorC", {"center": v(-4, -52) * mm, "radius": 3 * mm});
            skLineSegment(sketch, "E352.MirrorCS", {"start": v(-69.98, -36) * mm, "end": v(69.98, -36) * mm, "construction": true});
            skCircle(sketch, "E353.MirrorC", {"center": v(12, -20) * mm, "radius": 3 * mm});
            skCircle(sketch, "E354.MirrorC", {"center": v(60, -52) * mm, "radius": 3 * mm});
            skCircle(sketch, "E355.MirrorC", {"center": v(-36, -20) * mm, "radius": 3 * mm});
            skCircle(sketch, "E356.MirrorC", {"center": v(-68, -28) * mm, "radius": 3 * mm});
            skCircle(sketch, "E357.MirrorC", {"center": v(60, -20) * mm, "radius": 3 * mm});
            skCircle(sketch, "E358.MirrorC", {"center": v(28, -28) * mm, "radius": 3 * mm});
            skLineSegment(sketch, "E359.MirrorCS", {"start": v(-70.89, -76) * mm, "end": v(70.89, -76) * mm, "construction": true});
            skCircle(sketch, "E360.MirrorC", {"center": v(-20, -28) * mm, "radius": 3 * mm});
            skCircle(sketch, "E361.MirrorC", {"center": v(68, -28) * mm, "radius": 3 * mm});
            skCircle(sketch, "E362.MirrorC", {"center": v(-12, -44) * mm, "radius": 3 * mm});
            skLineSegment(sketch, "E363.MirrorCS", {"start": v(-69.98, -68) * mm, "end": v(69.98, -68) * mm, "construction": true});
            skCircle(sketch, "E364.MirrorC", {"center": v(-12, -60) * mm, "radius": 3 * mm});
            skCircle(sketch, "E365.MirrorC", {"center": v(-28, -20) * mm, "radius": 3 * mm});
            skCircle(sketch, "E366.MirrorC", {"center": v(68, -52) * mm, "radius": 3 * mm});
            skCircle(sketch, "E367.MirrorC", {"center": v(-12, -28) * mm, "radius": 3 * mm});
            skCircle(sketch, "E368.MirrorC", {"center": v(36, -60) * mm, "radius": 3 * mm});
            skCircle(sketch, "E369.MirrorC", {"center": v(-60, -76) * mm, "radius": 3 * mm});
            skCircle(sketch, "E370.MirrorC", {"center": v(28, -60) * mm, "radius": 3 * mm});
            skCircle(sketch, "E371.MirrorC", {"center": v(-44, -44) * mm, "radius": 3 * mm});
            skCircle(sketch, "E372.MirrorC", {"center": v(44, -76) * mm, "radius": 3 * mm});
            skLineSegment(sketch, "E373.MirrorCS", {"start": v(-69.98, -20) * mm, "end": v(69.98, -20) * mm, "construction": true});
            skLineSegment(sketch, "E374.MirrorCS", {"start": v(-68.12, -12) * mm, "end": v(68.12, -12) * mm});
            skCircle(sketch, "E375.MirrorC", {"center": v(-4, -12) * mm, "radius": 3 * mm});
            skCircle(sketch, "E376.MirrorC", {"center": v(20, -12) * mm, "radius": 3 * mm});
            skCircle(sketch, "E377.MirrorC", {"center": v(-20, -12) * mm, "radius": 3 * mm});
            skCircle(sketch, "E378.MirrorC", {"center": v(-44, -12) * mm, "radius": 3 * mm});
            skCircle(sketch, "E379.MirrorC", {"center": v(-68, -12) * mm, "radius": 3 * mm});
            skCircle(sketch, "E380.MirrorC", {"center": v(12, -12) * mm, "radius": 3 * mm});
            skCircle(sketch, "E381.MirrorC", {"center": v(60, -12) * mm, "radius": 3 * mm});
            skCircle(sketch, "E382.MirrorC", {"center": v(68, -12) * mm, "radius": 3 * mm});
            skCircle(sketch, "E383.MirrorC", {"center": v(-52, -12) * mm, "radius": 3 * mm});
            skCircle(sketch, "E384.MirrorC", {"center": v(-36, -12) * mm, "radius": 3 * mm});
            skCircle(sketch, "E385.MirrorC", {"center": v(28, -12) * mm, "radius": 3 * mm});
            skCircle(sketch, "E386.MirrorC", {"center": v(4, -12) * mm, "radius": 3 * mm});
            skCircle(sketch, "E387.MirrorC", {"center": v(44, -12) * mm, "radius": 3 * mm});
            skCircle(sketch, "E388.MirrorC", {"center": v(-12, -12) * mm, "radius": 3 * mm});
            skCircle(sketch, "E389.MirrorC", {"center": v(36, -12) * mm, "radius": 3 * mm});
            skCircle(sketch, "E390.MirrorC", {"center": v(-60, -12) * mm, "radius": 3 * mm});
            skCircle(sketch, "E391.MirrorC", {"center": v(52, -12) * mm, "radius": 3 * mm});
            skCircle(sketch, "E392.MirrorC", {"center": v(-28, -12) * mm, "radius": 3 * mm});
            skSolve(sketch);
        }
        {
            var Q0;
            Q0 = qSketchRegion(id + "F2", true);
            extrude(context, id + "F3", {"entities" : qUnion([Q0]), "operationType" : NewBodyOperationType.REMOVE, "oppositeDirection" : true, "depth" : 5 * mm, "offsetDistance" : 25 * mm});
        }
    });
